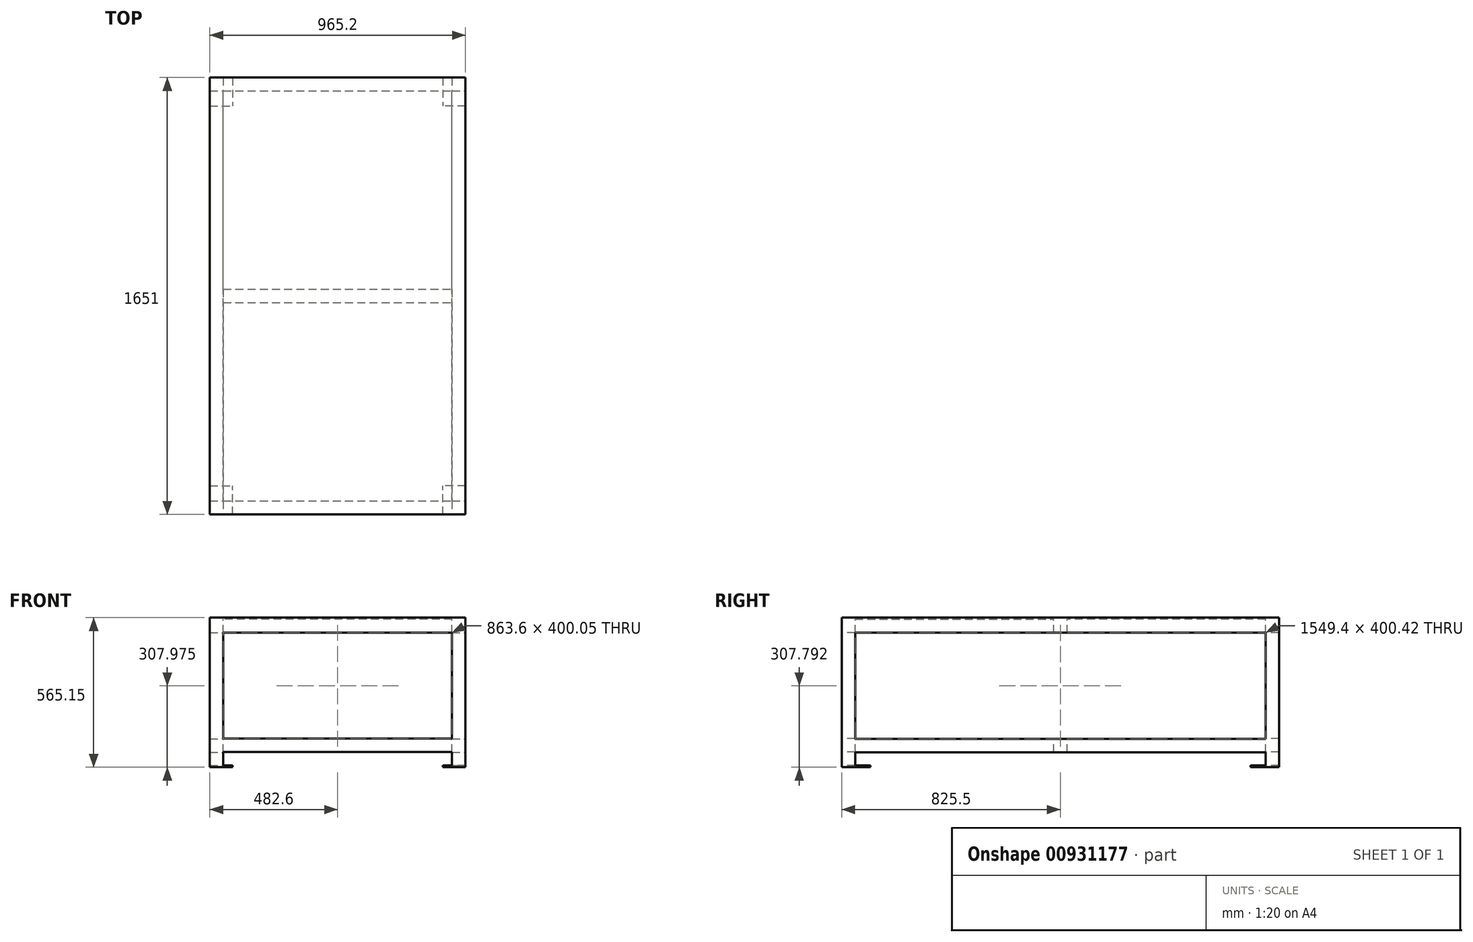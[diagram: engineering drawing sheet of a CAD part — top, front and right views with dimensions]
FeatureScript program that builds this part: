
annotation { "Feature Type Name" : "Feature", "Feature Type Description" : "" }
export const myFeature = defineFeature(function(context is Context, id is Id, definition is map)
    precondition{}
    {
        {
            var Q0;
            Q0=qCreatedBy(makeId("Front.planeOp"),FACE);
            var sketch = newSketch(context, id + "F0", { "sketchPlane" : qUnion([Q0])});
            skLineSegment(sketch, "E0.bottom", {"start": v(0, 0) * mm, "end": v(965.2, 0) * mm});
            skLineSegment(sketch, "E0.top", {"start": v(0, 552.45) * mm, "end": v(965.2, 552.45) * mm});
            skLineSegment(sketch, "E0.left", {"start": v(0, 0) * mm, "end": v(0, 552.45) * mm});
            skLineSegment(sketch, "E0.right", {"start": v(965.2, 0) * mm, "end": v(965.2, 552.45) * mm});
            skSolve(sketch);
        }
        {
            var Q0;
            Q0 = qSketchRegion(id + "F0", true);
            extrude(context, id + "F1", {"entities" : qUnion([Q0]), "oppositeDirection" : true, "depth" : 1651 * mm, "offsetDistance" : 25.4 * mm});
        }
        {
            var Q0;
            Q0=makeQuery(id+"F1.opExtrude","CAP_FACE",FACE,{"disambiguationData":[OSD([sQuery(id+"F0.wireOp",EDGE,"E0.bottom"),sQuery(id+"F0.wireOp",EDGE,"E0.top"),sQuery(id+"F0.wireOp",EDGE,"E0.left"),sQuery(id+"F0.wireOp",EDGE,"E0.right")])],"isStart":true});
            var sketch = newSketch(context, id + "F2", { "sketchPlane" : qUnion([Q0])});
            skLineSegment(sketch, "E1.bottom", {"start": v(50.8, 0) * mm, "end": v(914.4, 0) * mm});
            skLineSegment(sketch, "E1.top", {"start": v(50.8, 50.8) * mm, "end": v(914.4, 50.8) * mm});
            skLineSegment(sketch, "E1.left", {"start": v(50.8, 0) * mm, "end": v(50.8, 50.8) * mm});
            skLineSegment(sketch, "E1.right", {"start": v(914.4, 0) * mm, "end": v(914.4, 50.8) * mm});
            skLineSegment(sketch, "E2.bottom", {"start": v(50.8, 101.6) * mm, "end": v(914.4, 101.6) * mm});
            skLineSegment(sketch, "E2.top", {"start": v(50.8, 501.65) * mm, "end": v(914.4, 501.65) * mm});
            skLineSegment(sketch, "E2.left", {"start": v(50.8, 101.6) * mm, "end": v(50.8, 501.65) * mm});
            skLineSegment(sketch, "E2.right", {"start": v(914.4, 101.6) * mm, "end": v(914.4, 501.65) * mm});
            skSolve(sketch);
        }
        {
            var Q0;
            Q0 = qSketchRegion(id + "F2", true);
            extrude(context, id + "F3", {"entities" : qUnion([Q0]), "operationType" : NewBodyOperationType.REMOVE, "endBound" : BoundingType.UP_TO_NEXT, "oppositeDirection" : true, "depth" : 25.4 * mm, "offsetDistance" : 25.4 * mm});
        }
        {
            var Q0;
            Q0=makeQuery(id+"F1.opExtrude","SWEPT_FACE",FACE,{"disambiguationData":[OSD([sQuery(id+"F0.wireOp",EDGE,"E0.right")])]});
            var sketch = newSketch(context, id + "F4", { "sketchPlane" : qUnion([Q0])});
            skLineSegment(sketch, "E3.bottom", {"start": v(50.8, 0) * mm, "end": v(1600.2, 0) * mm});
            skLineSegment(sketch, "E3.top", {"start": v(50.8, 50.43) * mm, "end": v(1600.2, 50.43) * mm});
            skLineSegment(sketch, "E3.left", {"start": v(50.8, 0) * mm, "end": v(50.8, 50.43) * mm});
            skLineSegment(sketch, "E3.right", {"start": v(1600.2, 0) * mm, "end": v(1600.2, 50.43) * mm});
            skLineSegment(sketch, "E4.bottom", {"start": v(50.8, 101.23) * mm, "end": v(1600.2, 101.23) * mm});
            skLineSegment(sketch, "E4.top", {"start": v(50.8, 501.65) * mm, "end": v(1600.2, 501.65) * mm});
            skLineSegment(sketch, "E4.left", {"start": v(50.8, 101.23) * mm, "end": v(50.8, 501.65) * mm});
            skLineSegment(sketch, "E4.right", {"start": v(1600.2, 101.23) * mm, "end": v(1600.2, 501.65) * mm});
            skSolve(sketch);
        }
        {
            var Q0;
            Q0 = qSketchRegion(id + "F4", true);
            var Q1;
            Q1=makeQuery(id+"F1.opExtrude","SWEPT_FACE",FACE,{"disambiguationData":[OSD([sQuery(id+"F0.wireOp",EDGE,"E0.left")])]});
            extrude(context, id + "F5", {"entities" : qUnion([Q0]), "operationType" : NewBodyOperationType.REMOVE, "endBound" : BoundingType.UP_TO_SURFACE, "oppositeDirection" : true, "depth" : 25.4 * mm, "endBoundEntityFace" : qUnion([Q1]), "offsetDistance" : 25.4 * mm});
        }
        {
            var Q0;
            Q0=makeQuery(id+"F1.opExtrude","SWEPT_FACE",FACE,{"disambiguationData":[OSD([sQuery(id+"F0.wireOp",EDGE,"E0.top")])]});
            var sketch = newSketch(context, id + "F6", { "sketchPlane" : qUnion([Q0])});
            skLineSegment(sketch, "E5.bottom", {"start": v(914.4, 50.8) * mm, "end": v(50.8, 50.8) * mm});
            skLineSegment(sketch, "E5.top", {"start": v(914.4, 800.1) * mm, "end": v(50.8, 800.1) * mm});
            skLineSegment(sketch, "E5.left", {"start": v(914.4, 50.8) * mm, "end": v(914.4, 800.1) * mm});
            skLineSegment(sketch, "E5.right", {"start": v(50.8, 50.8) * mm, "end": v(50.8, 800.1) * mm});
            skLineSegment(sketch, "E6", {"start": v(965.2, 825.5) * mm, "end": v(0, 825.5) * mm, "construction": true});
            skLineSegment(sketch, "E7.MirrorCS", {"start": v(914.4, 850.9) * mm, "end": v(50.8, 850.9) * mm});
            skLineSegment(sketch, "E8.MirrorCS", {"start": v(914.4, 1600.2) * mm, "end": v(914.4, 850.9) * mm});
            skLineSegment(sketch, "E9.MirrorCS", {"start": v(50.8, 1600.2) * mm, "end": v(50.8, 850.9) * mm});
            skLineSegment(sketch, "E10.MirrorCS", {"start": v(914.4, 1600.2) * mm, "end": v(50.8, 1600.2) * mm});
            skSolve(sketch);
        }
        {
            var Q0;
            Q0 = qSketchRegion(id + "F6", true);
            extrude(context, id + "F7", {"entities" : qUnion([Q0]), "operationType" : NewBodyOperationType.REMOVE, "oppositeDirection" : true, "depth" : 508 * mm, "offsetDistance" : 25.4 * mm});
        }
        {
            var Q0;
            {var subQ0=sQuery(id+"F0.wireOp",EDGE,"E0.right");var subQ3=sQuery(id+"F0.wireOp",EDGE,"E0.bottom");var subQ5=makeQuery(id+"F1.opExtrude","SWEPT_FACE",FACE,{"disambiguationData":[OSD([subQ0])]});Q0=makeQuery(id+"F5.boolean.opBoolean","SPLIT",FACE,{"disambiguationData":[TD([makeQuery(id+"F5.opExtrude","SWEPT_FACE",FACE,{"disambiguationData":[OSD([sQuery(id+"F4.wireOp",EDGE,"E3.right")])]})])],"derivedFrom":makeQuery(id+"F3.boolean.opBoolean","SPLIT",FACE,{"disambiguationData":[TD([subQ5])],"derivedFrom":makeQuery(id+"F1.opExtrude","SWEPT_FACE",FACE,{"disambiguationData":[OSD([subQ3])]})})});}
            var sketch = newSketch(context, id + "F8", { "sketchPlane" : qUnion([Q0])});
            skLineSegment(sketch, "E11", {"start": v(482.6, -1651) * mm, "end": v(482.6, -825.5) * mm, "construction": true});
            skLineSegment(sketch, "E12", {"start": v(965.65, -825.5) * mm, "end": v(0, -825.5) * mm, "construction": true});
            skLineSegment(sketch, "E13.bottom", {"start": v(965.2, -1651) * mm, "end": v(879.48, -1651) * mm});
            skLineSegment(sketch, "E13.top", {"start": v(965.2, -1543.05) * mm, "end": v(879.48, -1543.05) * mm});
            skLineSegment(sketch, "E13.left", {"start": v(965.2, -1651) * mm, "end": v(965.2, -1543.05) * mm});
            skLineSegment(sketch, "E13.right", {"start": v(879.48, -1651) * mm, "end": v(879.48, -1543.05) * mm});
            skLineSegment(sketch, "E14.MirrorCS", {"start": v(85.72, -1651) * mm, "end": v(85.72, -1543.05) * mm});
            skLineSegment(sketch, "E15.MirrorCS", {"start": v(0, -1543.05) * mm, "end": v(85.73, -1543.05) * mm});
            skLineSegment(sketch, "E16.MirrorCS", {"start": v(0, -1651) * mm, "end": v(0, -1543.05) * mm});
            skLineSegment(sketch, "E17.MirrorCS", {"start": v(0, -1651) * mm, "end": v(85.73, -1651) * mm});
            skLineSegment(sketch, "E18.MirrorCS", {"start": v(965.2, -107.95) * mm, "end": v(879.47, -107.95) * mm});
            skLineSegment(sketch, "E19.MirrorCS", {"start": v(879.47, 0) * mm, "end": v(879.47, -107.95) * mm});
            skLineSegment(sketch, "E20.MirrorCS", {"start": v(965.2, 0) * mm, "end": v(965.2, -107.95) * mm});
            skLineSegment(sketch, "E21.MirrorCS", {"start": v(965.2, 0) * mm, "end": v(879.47, 0) * mm});
            skLineSegment(sketch, "E22.MirrorCS", {"start": v(85.72, 0) * mm, "end": v(85.72, -107.95) * mm});
            skLineSegment(sketch, "E23.MirrorCS", {"start": v(0, -107.95) * mm, "end": v(85.72, -107.95) * mm});
            skLineSegment(sketch, "E24.MirrorCS", {"start": v(0, 0) * mm, "end": v(0, -107.95) * mm});
            skLineSegment(sketch, "E25.MirrorCS", {"start": v(0, 0) * mm, "end": v(85.72, 0) * mm});
            skSolve(sketch);
        }
        {
            var Q0;
            Q0 = qSketchRegion(id + "F8", true);
            extrude(context, id + "F9", {"entities" : qUnion([Q0]), "operationType" : NewBodyOperationType.ADD, "depth" : 6.35 * mm, "offsetDistance" : 25.4 * mm});
        }
        {
            var Q0;
            Q0=makeQuery(id+"F9.boolean.opBoolean","MERGE",FACE,{"derivedFrom":[makeQuery(id+"F1.opExtrude","SWEPT_FACE",FACE,{"disambiguationData":[OSD([sQuery(id+"F0.wireOp",EDGE,"E0.right")])]}),makeQuery(id+"F9.opExtrude","SWEPT_FACE",FACE,{"disambiguationData":[OSD([sQuery(id+"F8.wireOp",EDGE,"E13.left")])]}),makeQuery(id+"F9.opExtrude","SWEPT_FACE",FACE,{"disambiguationData":[OSD([sQuery(id+"F8.wireOp",EDGE,"E20.MirrorCS")])]})]});
            var sketch = newSketch(context, id + "F10", { "sketchPlane" : qUnion([Q0])});
            skLineSegment(sketch, "E26.bottom", {"start": v(0, 552.45) * mm, "end": v(1651, 552.45) * mm});
            skLineSegment(sketch, "E26.top", {"start": v(0, 558.8) * mm, "end": v(1651, 558.8) * mm});
            skLineSegment(sketch, "E26.left", {"start": v(0, 552.45) * mm, "end": v(0, 558.8) * mm});
            skLineSegment(sketch, "E26.right", {"start": v(1651, 552.45) * mm, "end": v(1651, 558.8) * mm});
            skSolve(sketch);
        }
        {
            var Q0;
            Q0 = qSketchRegion(id + "F10", true);
            extrude(context, id + "F11", {"entities" : qUnion([Q0]), "operationType" : NewBodyOperationType.ADD, "oppositeDirection" : true, "depth" : 965.2 * mm, "offsetDistance" : 25.4 * mm});
        }
    });
